# Revit family: LNC2
name_source: partatom
category: Lighting Fixtures
units: mm (PartAtom-declared; Revit-internal decimal feet)

## family parameters
Cut with Voids When Loaded = No
Host = Face
Light Source = No
OmniClass Number = 23.80.70.11
OmniClass Title = Luminaries for Internal Lighting
Part Type = Normal
Room Calculation Point = No
Round Connector Dimension = Use Diameter
Shared = No

## types (5) — shared parameters
Apparent Load = 0 VA
Default Elevation = 48.000"
Description = The LNC2 has 60% more lumens and increased performance than smaller LNC models. The LNC2 achieves up to 85% energy savings over traditional lighting sources
Glass = White Glass
Lamp = LED Lamp
Manufacturer = EXO
Manufacturer Fax = (866)-898-1065
Model = LNC2
URL = https://www.currentlighting.com
Voltage = 120 V
Wattage Comments = 29-45W

## per-type parameters (varying)
| type | Backbox | Photometric Web |
| Bronze | Metal - Bronze | Web LNC2 : LNC2-12LU-3K-3, 12 LED, 3000K, TYPE 3 |
| White | Metal  - White | Web LNC2 : LNC2-12LU-3K-3, 12 LED, 3000K, TYPE 3 |
| Gray | Metal  - Gray | Web LNC2 : LNC2-12LU-3K-3, 12 LED, 3000K, TYPE 3 |
| Black | Metal  - Black | Web LNC2 : LNC2-12LU-5K-4, 12 LED, 5100K, TYPE 4 |
| Platinum | Metal - Platinum | Web LNC2 : LNC2-12LU-3K-3, 12 LED, 3000K, TYPE 3 |

## geometry (parser evidence)
native form markers: Blend x8, Sweep x4
no freeform markers — native parametric forms only
